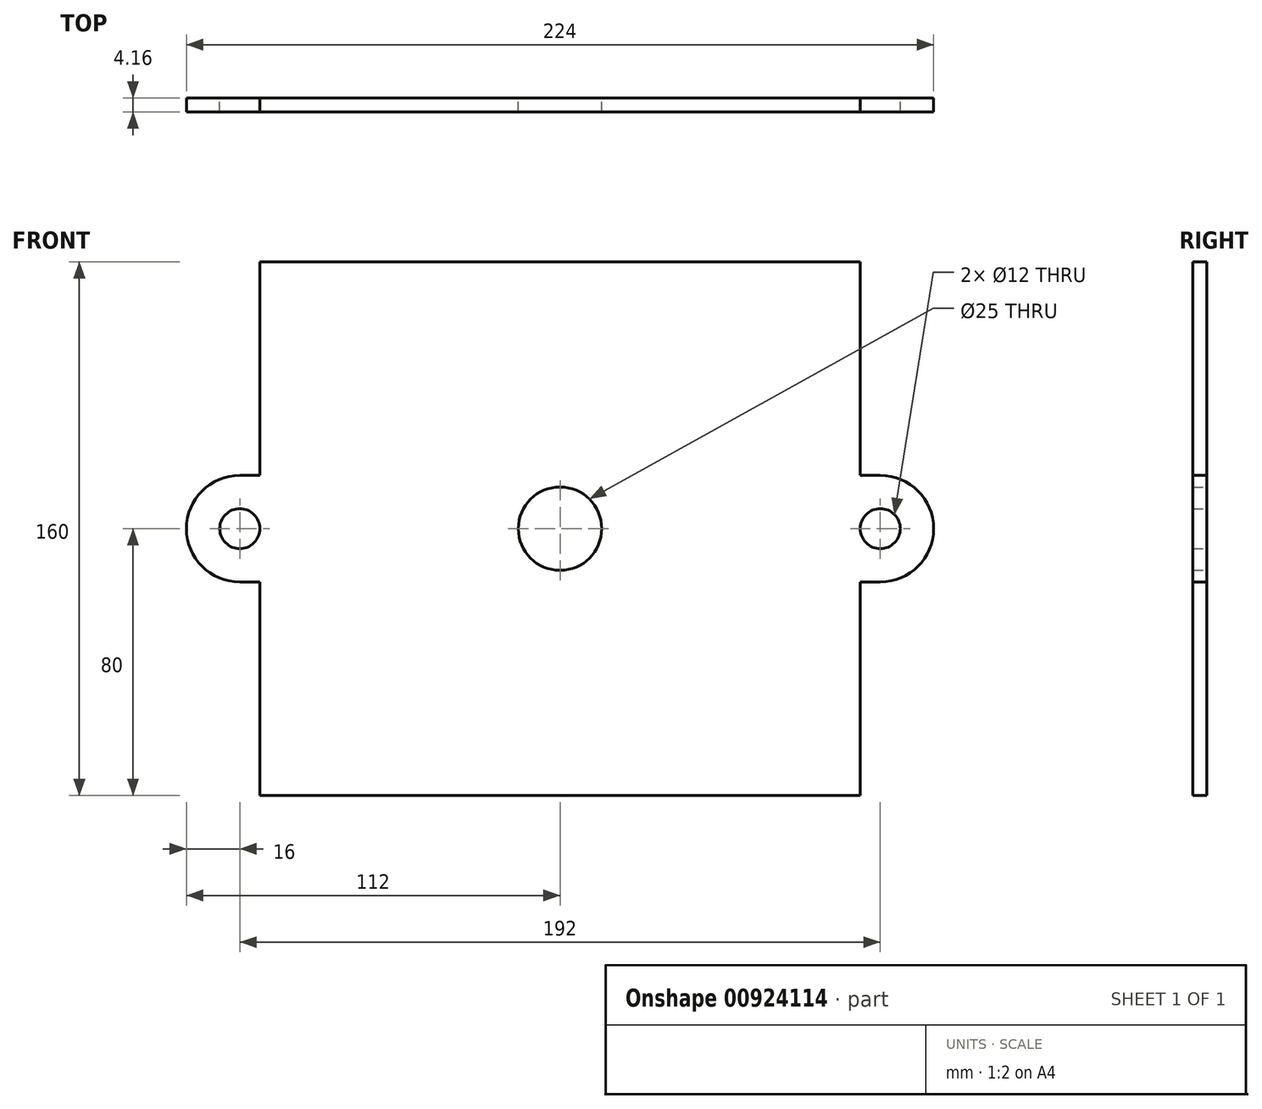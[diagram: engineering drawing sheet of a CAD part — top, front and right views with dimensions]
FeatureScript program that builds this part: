
annotation { "Feature Type Name" : "Feature", "Feature Type Description" : "" }
export const myFeature = defineFeature(function(context is Context, id is Id, definition is map)
    precondition{}
    {
        {
            var Q0;
            Q0=qCreatedBy(makeId("Front.planeOp"),FACE);
            var sketch = newSketch(context, id + "F0", { "sketchPlane" : qUnion([Q0])});
            skLineSegment(sketch, "E0.bottom", {"start": v(90, 80) * mm, "end": v(-90, 80) * mm});
            skLineSegment(sketch, "E0.top", {"start": v(90, -80) * mm, "end": v(-90, -80) * mm});
            skLineSegment(sketch, "E0.left", {"start": v(90, 80) * mm, "end": v(90, 16) * mm});
            skLineSegment(sketch, "E0.right", {"start": v(-90, 80) * mm, "end": v(-90, 16) * mm});
            skPoint(sketch, "E0.middle", {"position": v(0, 0) * mm});
            skCircle(sketch, "E1", {"center": v(-96, 0) * mm, "radius": 6 * mm});
            skCircle(sketch, "E2", {"center": v(96, 0) * mm, "radius": 6 * mm});
            skArc(sketch, "E3", {"start": v(-96, 16) * mm, "mid": v(-112, 0) * mm, "end": v(-96, -16) * mm});
            skArc(sketch, "E4", {"start": v(96, -16) * mm, "mid": v(112, 0) * mm, "end": v(96, 16) * mm});
            skLineSegment(sketch, "E5", {"start": v(-96, 16) * mm, "end": v(-90, 16) * mm});
            skLineSegment(sketch, "E6", {"start": v(96, 16) * mm, "end": v(90, 16) * mm});
            skLineSegment(sketch, "E7", {"start": v(96, -16) * mm, "end": v(90, -16) * mm});
            skLineSegment(sketch, "E8", {"start": v(-96, -16) * mm, "end": v(-90, -16) * mm});
            skLineSegment(sketch, "E9.trimOffspring", {"start": v(-90, -16) * mm, "end": v(-90, -80) * mm});
            skLineSegment(sketch, "E10.trimOffspring", {"start": v(90, -16) * mm, "end": v(90, -80) * mm});
            skCircle(sketch, "E11", {"center": v(0, 0) * mm, "radius": 12.5 * mm});
            skSolve(sketch);
        }
        {
            var Q0;
            Q0=makeQuery(id+"F0.imprint","IMPRINT",FACE,{"disambiguationData":[TD([[makeQuery(id+"F0.imprint","IMPRINT",EDGE,{"derivedFrom":sQuery(id+"F0.wireOp",EDGE,"E0.bottom")}),1.0]])]});
            extrude(context, id + "F1", {"entities" : qUnion([Q0]), "depth" : 2.08 * mm, "offsetDistance" : 25 * mm, "hasSecondDirection" : true, "secondDirectionOppositeDirection" : true, "secondDirectionDepth" : 2.08 * mm});
        }
    });
